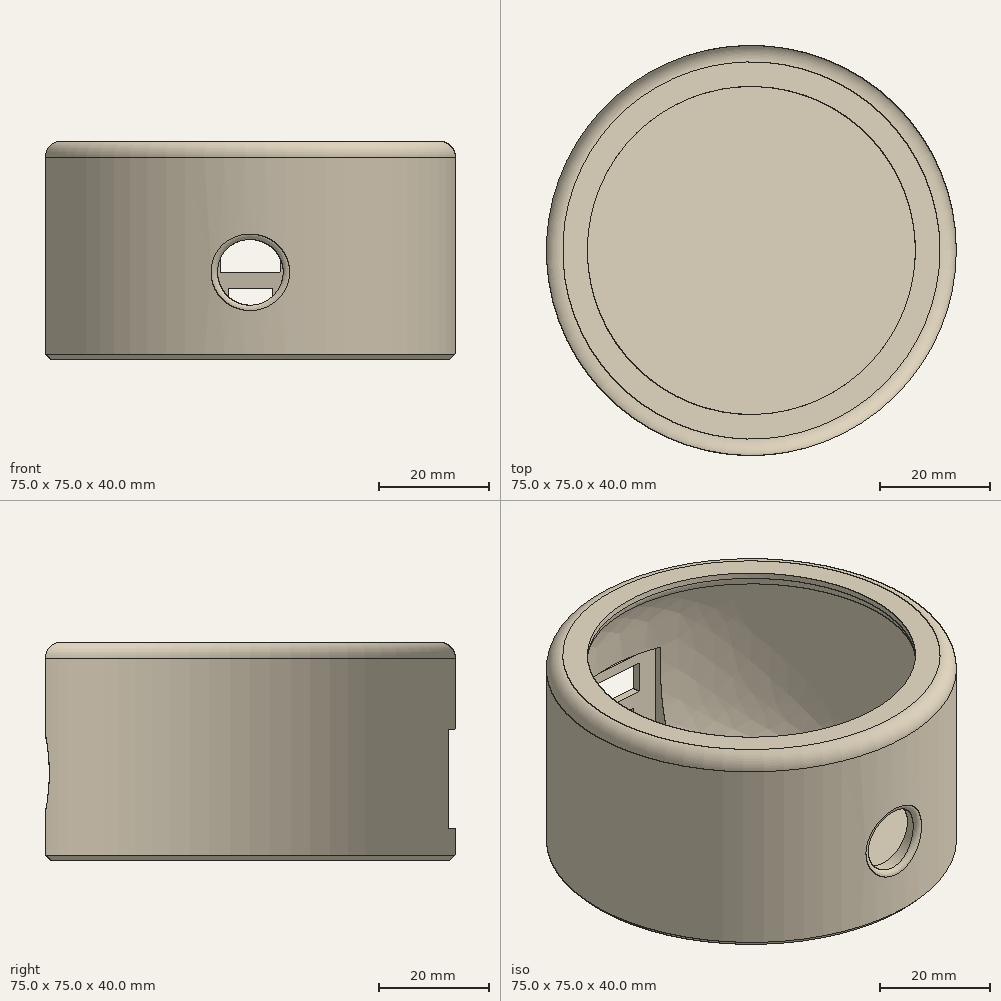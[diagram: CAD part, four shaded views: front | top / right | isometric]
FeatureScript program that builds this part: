
annotation { "Feature Type Name" : "Feature", "Feature Type Description" : "" }
export const myFeature = defineFeature(function(context is Context, id is Id, definition is map)
    precondition{}
    {
        {
            var Q0;
            Q0=qCreatedBy(makeId("Front.planeOp"),FACE);
            var sketch = newSketch(context, id + "F0", { "sketchPlane" : qUnion([Q0])});
            skEllipse(sketch, "E0", {"center": v(-30, 0) * mm, "majorRadius": 17.5 * mm, "minorRadius": 5 * mm, "majorAxis": v(0, -1)});
            skLineSegment(sketch, "E1", {"start": v(-30, 0) * mm, "end": v(0, 0) * mm, "construction": true});
            skLineSegment(sketch, "E2.bottom", {"start": v(-37.5, -20) * mm, "end": v(37.5, -20) * mm});
            skLineSegment(sketch, "E2.top", {"start": v(-37.5, 20) * mm, "end": v(37.5, 20) * mm});
            skLineSegment(sketch, "E2.left", {"start": v(-37.5, -20) * mm, "end": v(-37.5, 20) * mm});
            skLineSegment(sketch, "E2.right", {"start": v(37.5, -20) * mm, "end": v(37.5, 20) * mm});
            skPoint(sketch, "E2.middle", {"position": v(0, 0) * mm});
            skPoint(sketch, "E3.startSnap0", {"position": v(0, -20) * mm});
            skLineSegment(sketch, "E4", {"start": v(0, 0) * mm, "end": v(0, 20) * mm, "construction": true});
            skPoint(sketch, "E5.1.internal.snap0", {"position": v(-30, 17.5) * mm});
            skLineSegment(sketch, "E6", {"start": v(-30, 17.5) * mm, "end": v(-30, 20) * mm});
            skLineSegment(sketch, "E7", {"start": v(-30, -17.5) * mm, "end": v(0, -17.5) * mm});
            skLineSegment(sketch, "E8", {"start": v(0, -17.5) * mm, "end": v(0, -20) * mm});
            skCircle(sketch, "E9", {"center": v(0, -4) * mm, "radius": 6 * mm});
            skLineSegment(sketch, "E10", {"start": v(-30, 0) * mm, "end": v(-35, 0) * mm, "construction": true});
            skLineSegment(sketch, "E11", {"start": v(0, 0) * mm, "end": v(0, -4) * mm, "construction": true});
            skCircle(sketch, "E12", {"center": v(0, -4) * mm, "radius": 5.5 * mm});
            skSolve(sketch);
        }
        {
            var Q0;
            {var subQ0=sQuery(id+"F0.wireOp",EDGE,"E2.left");Q0=makeQuery(id+"F0.imprint","IMPRINT",FACE,{"disambiguationData":[TD([[makeQuery(id+"F0.imprint","IMPRINT",EDGE,{"derivedFrom":subQ0}),-1.0]])]});}
            var Q1;
            Q1=sQuery(id+"F0.wireOp",EDGE,"E4");
            revolve(context, id + "F1", {"entities" : qUnion([Q0]), "axis" : qUnion([Q1]), "revolveType" : RevolveType.FULL});
        }
        {
            var Q0;
            Q0=makeQuery(id+"F1.opRevolve","SWEPT_EDGE",EDGE,{"disambiguationData":[OSD([sQuery(id+"F0.wireOp",EDGE,"E2.top"),sQuery(id+"F0.wireOp",EDGE,"E2.left")])]});
            fillet(context, id + "F2", {"entities" : qUnion([Q0]), "radius" : 3 * mm, "tangentPropagation" : true, "allowEdgeOverflow" : false});
        }
        {
            var Q0;
            Q0=makeQuery(id+"F1.opRevolve","SWEPT_EDGE",EDGE,{"disambiguationData":[OSD([sQuery(id+"F0.wireOp",EDGE,"E2.bottom"),sQuery(id+"F0.wireOp",EDGE,"E2.left")])]});
            chamfer(context, id + "F3", {"entities" : qUnion([Q0]), "width" : 1 * mm, "tangentPropagation" : true});
        }
        {
            var Q0;
            Q0=makeQuery(id+"F1.opRevolve","SWEPT_EDGE",EDGE,{"disambiguationData":[OSD([sQuery(id+"F0.wireOp",EDGE,"E0"),sQuery(id+"F0.wireOp",EDGE,"E6")])]});
            fillet(context, id + "F4", {"entities" : qUnion([Q0]), "radius" : 2 * mm, "tangentPropagation" : true, "allowEdgeOverflow" : false});
        }
        {
            var Q0;
            Q0=makeQuery(id+"F0.imprint","IMPRINT",FACE,{"disambiguationData":[TD([[makeQuery(id+"F0.imprint","IMPRINT",EDGE,{"derivedFrom":sQuery(id+"F0.wireOp",EDGE,"E9")}),1.0]])]});
            var Q1;
            Q1=makeQuery(id+"F0.imprint","IMPRINT",FACE,{"disambiguationData":[TD([[makeQuery(id+"F0.imprint","IMPRINT",EDGE,{"derivedFrom":sQuery(id+"F0.wireOp",EDGE,"E12")}),1.0]])]});
            extrude(context, id + "F5", {"entities" : qUnion([Q0, Q1]), "operationType" : NewBodyOperationType.REMOVE, "depth" : 43.8 * mm});
        }
        {
            var Q0;
            Q0=makeQuery(id+"F5.boolean.opBoolean","INTERSECT",EDGE,{"derivedFrom":[makeQuery(id+"F1.opRevolve","SWEPT_FACE",FACE,{"disambiguationData":[OSD([sQuery(id+"F0.wireOp",EDGE,"E2.left")])]}),makeQuery(id+"F5.opExtrude","SWEPT_FACE",FACE,{"disambiguationData":[OSD([sQuery(id+"F0.wireOp",EDGE,"E9")])]})]});
            fillet(context, id + "F6", {"entities" : qUnion([Q0]), "radius" : 1 * mm, "tangentPropagation" : true, "allowEdgeOverflow" : false});
        }
        {
            var Q0;
            Q0=qCreatedBy(makeId("Front.planeOp"),FACE);
            cPlane(context, id + "F7", {"entities" : qUnion([Q0]), "cplaneType" : CPlaneType.OFFSET, "offset" : 37.5 * mm, "oppositeDirection" : true, "width" : 150 * mm, "height" : 150 * mm});
        }
        {
            var Q0;
            Q0=qCreatedBy(id+"F7.planeOp",FACE);
            var sketch = newSketch(context, id + "F8", { "sketchPlane" : qUnion([Q0])});
            skLineSegment(sketch, "E13.bottom", {"start": v(10, 4) * mm, "end": v(-10, 4) * mm});
            skLineSegment(sketch, "E13.top", {"start": v(10, -14) * mm, "end": v(-10, -14) * mm});
            skLineSegment(sketch, "E13.left", {"start": v(10, 4) * mm, "end": v(10, -14) * mm});
            skLineSegment(sketch, "E13.right", {"start": v(-10, 4) * mm, "end": v(-10, -14) * mm});
            skLineSegment(sketch, "E14", {"start": v(0, 0) * mm, "end": v(0, -14) * mm, "construction": true});
            skLineSegment(sketch, "E15.bottom", {"start": v(4, -7) * mm, "end": v(-4, -7) * mm});
            skLineSegment(sketch, "E15.top", {"start": v(4, -10) * mm, "end": v(-4, -10) * mm});
            skLineSegment(sketch, "E15.left", {"start": v(4, -7) * mm, "end": v(4, -10) * mm});
            skLineSegment(sketch, "E15.right", {"start": v(-4, -7) * mm, "end": v(-4, -10) * mm});
            skLineSegment(sketch, "E16", {"start": v(0, 0) * mm, "end": v(0, -10) * mm, "construction": true});
            skLineSegment(sketch, "E17.bottom", {"start": v(5.5, 2) * mm, "end": v(-5.5, 2) * mm});
            skLineSegment(sketch, "E17.top", {"start": v(5.5, -4) * mm, "end": v(-5.5, -4) * mm});
            skLineSegment(sketch, "E17.left", {"start": v(5.5, 2) * mm, "end": v(5.5, -4) * mm});
            skLineSegment(sketch, "E17.right", {"start": v(-5.5, 2) * mm, "end": v(-5.5, -4) * mm});
            skLineSegment(sketch, "E18", {"start": v(0, 0) * mm, "end": v(0, -4) * mm, "construction": true});
            skSolve(sketch);
        }
        {
            var Q0;
            Q0=makeQuery(id+"F8.imprint","IMPRINT",FACE,{"disambiguationData":[TD([[makeQuery(id+"F8.imprint","IMPRINT",EDGE,{"derivedFrom":sQuery(id+"F8.wireOp",EDGE,"E13.bottom")}),1.0]])]});
            extrude(context, id + "F9", {"entities" : qUnion([Q0]), "operationType" : NewBodyOperationType.REMOVE, "depth" : 11 * mm});
        }
        {
            var Q0;
            Q0=qCreatedBy(id+"F7.planeOp",FACE);
            cPlane(context, id + "F10", {"entities" : qUnion([Q0]), "cplaneType" : CPlaneType.OFFSET, "offset" : 1.5 * mm, "width" : 150 * mm, "height" : 150 * mm});
        }
        {
            var Q0;
            Q0=qCreatedBy(id+"F10.planeOp",FACE);
            var sketch = newSketch(context, id + "F11", { "sketchPlane" : qUnion([Q0])});
            skLineSegment(sketch, "E19.bottom", {"start": v(9.77, 4) * mm, "end": v(-10.23, 4) * mm});
            skLineSegment(sketch, "E19.top", {"start": v(9.77, -14) * mm, "end": v(-10.23, -14) * mm});
            skLineSegment(sketch, "E19.left", {"start": v(9.77, 4) * mm, "end": v(9.77, -14) * mm});
            skLineSegment(sketch, "E19.right", {"start": v(-10.23, 4) * mm, "end": v(-10.23, -14) * mm});
            skLineSegment(sketch, "E20", {"start": v(0, 0) * mm, "end": v(0, -14) * mm, "construction": true});
            skSolve(sketch);
        }
        {
            var Q0;
            Q0=makeQuery(id+"F11.imprint","IMPRINT",FACE,{"disambiguationData":[TD([[makeQuery(id+"F11.imprint","IMPRINT",EDGE,{"derivedFrom":sQuery(id+"F11.wireOp",EDGE,"E19.bottom")}),1.0]])]});
            extrude(context, id + "F12", {"entities" : qUnion([Q0]), "operationType" : NewBodyOperationType.ADD, "depth" : 1.5 * mm});
        }
        {
            var Q0;
            Q0=makeQuery(id+"F8.imprint","IMPRINT",FACE,{"disambiguationData":[TD([[makeQuery(id+"F8.imprint","IMPRINT",EDGE,{"derivedFrom":sQuery(id+"F8.wireOp",EDGE,"E17.bottom")}),1.0]])]});
            var Q1;
            Q1=makeQuery(id+"F8.imprint","IMPRINT",FACE,{"disambiguationData":[TD([[makeQuery(id+"F8.imprint","IMPRINT",EDGE,{"derivedFrom":sQuery(id+"F8.wireOp",EDGE,"E15.bottom")}),1.0]])]});
            extrude(context, id + "F13", {"entities" : qUnion([Q0, Q1]), "operationType" : NewBodyOperationType.REMOVE, "depth" : 10 * mm});
        }
    });
